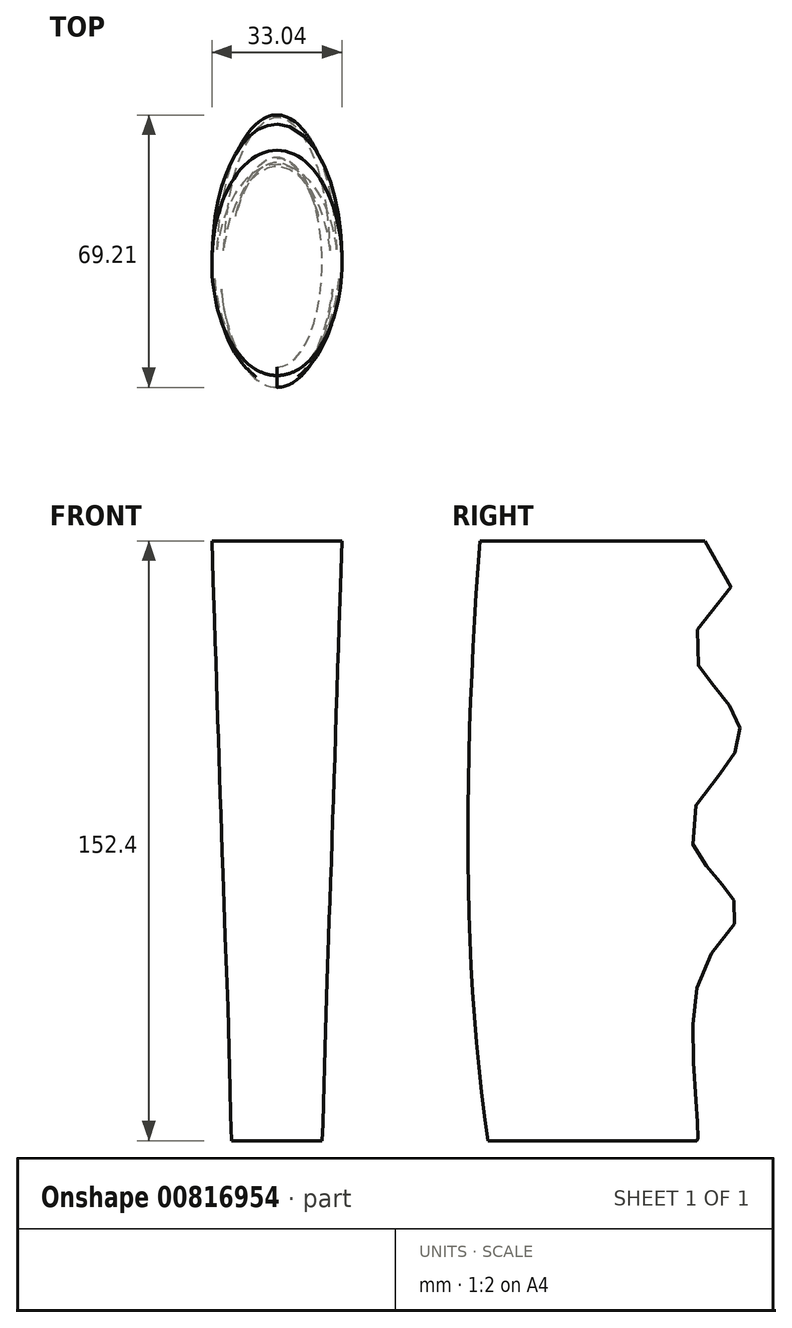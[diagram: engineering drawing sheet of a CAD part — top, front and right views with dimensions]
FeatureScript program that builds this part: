
annotation { "Feature Type Name" : "Feature", "Feature Type Description" : "" }
export const myFeature = defineFeature(function(context is Context, id is Id, definition is map)
    precondition{}
    {
        {
            var Q0;
            Q0=qCreatedBy(makeId("Top.planeOp"),FACE);
            var sketch = newSketch(context, id + "F0", { "sketchPlane" : qUnion([Q0])});
            skEllipse(sketch, "E0", {"center": v(0, 0) * mm, "majorRadius": 26.54 * mm, "minorRadius": 11.5 * mm, "majorAxis": v(0, 1)});
            skPoint(sketch, "E1", {"position": v(0, 26.54) * mm});
            skPoint(sketch, "E2", {"position": v(0, -26.54) * mm});
            skSolve(sketch);
        }
        {
            var Q0;
            Q0=qCreatedBy(makeId("Top.planeOp"),FACE);
            cPlane(context, id + "F1", {"entities" : qUnion([Q0]), "cplaneType" : CPlaneType.OFFSET, "offset" : 152.4 * mm, "width" : 152.4 * mm, "height" : 152.4 * mm});
        }
        {
            var Q0;
            Q0=qCreatedBy(id+"F1.planeOp",FACE);
            var sketch = newSketch(context, id + "F2", { "sketchPlane" : qUnion([Q0])});
            skEllipse(sketch, "E3", {"center": v(0, 0) * mm, "majorRadius": 28.62 * mm, "minorRadius": 16.52 * mm, "majorAxis": v(0, 1)});
            skPoint(sketch, "E4", {"position": v(0, 28.62) * mm});
            skPoint(sketch, "E5", {"position": v(0, -28.62) * mm});
            skSolve(sketch);
        }
        {
            var Q0;
            Q0=qCreatedBy(makeId("Right.planeOp"),FACE);
            var sketch = newSketch(context, id + "F3", { "sketchPlane" : qUnion([Q0])});
            skFitSpline(sketch, "E6", {"points": [v(-26.54, 0) * mm, v(-28.62, 152.4) * mm], "startDerivative": vector(-21.08, 139.96) * mm, "endDerivative": vector(11.3, 154.75) * mm});
            skFitSpline(sketch, "E7", {"points": [v(19.72, 13.99) * mm, v(26.15, 0.35) * mm, v(26.89, 40.14) * mm, v(36.93, 58.7) * mm, v(24.44, 79.68) * mm, v(37.56, 103.96) * mm, v(25.22, 127.24) * mm, v(28.62, 152.4) * mm], "startDerivative": vector(-3.5, 99.36) * mm, "endDerivative": vector(-333.21, 281.61) * mm});
            skSolve(sketch);
        }
        {
            var Q0;
            Q0=makeQuery(id+"F0.imprint","IMPRINT",FACE,{"disambiguationData":[TD([[makeQuery(id+"F0.imprint","IMPRINT",EDGE,{"derivedFrom":sQuery(id+"F0.wireOp",EDGE,"E0")}),1.0]])]});
            var Q1;
            Q1=makeQuery(id+"F2.imprint","IMPRINT",FACE,{"disambiguationData":[TD([[makeQuery(id+"F2.imprint","IMPRINT",EDGE,{"derivedFrom":sQuery(id+"F2.wireOp",EDGE,"E3")}),1.0]])]});
            var Q2;
            Q2=sQuery(id+"F3.wireOp",EDGE,"E6");
            var Q3;
            Q3=sQuery(id+"F3.wireOp",EDGE,"E7");
            loft(context, id + "F4", {"addGuides" : true, "sheetProfilesArray" : [{ "sheetProfileEntities" : qUnion([Q0]) }, { "sheetProfileEntities" : qUnion([Q1]) }], "guidesArray" : [{ "guideEntities" : qUnion([Q2]), "guideDerivativeType" : LoftGuideDerivativeType.DEFAULT, "guideDerivativeMagnitude" : 1 }, { "guideEntities" : qUnion([Q3]), "guideDerivativeType" : LoftGuideDerivativeType.DEFAULT, "guideDerivativeMagnitude" : 1 }]});
        }
    });
